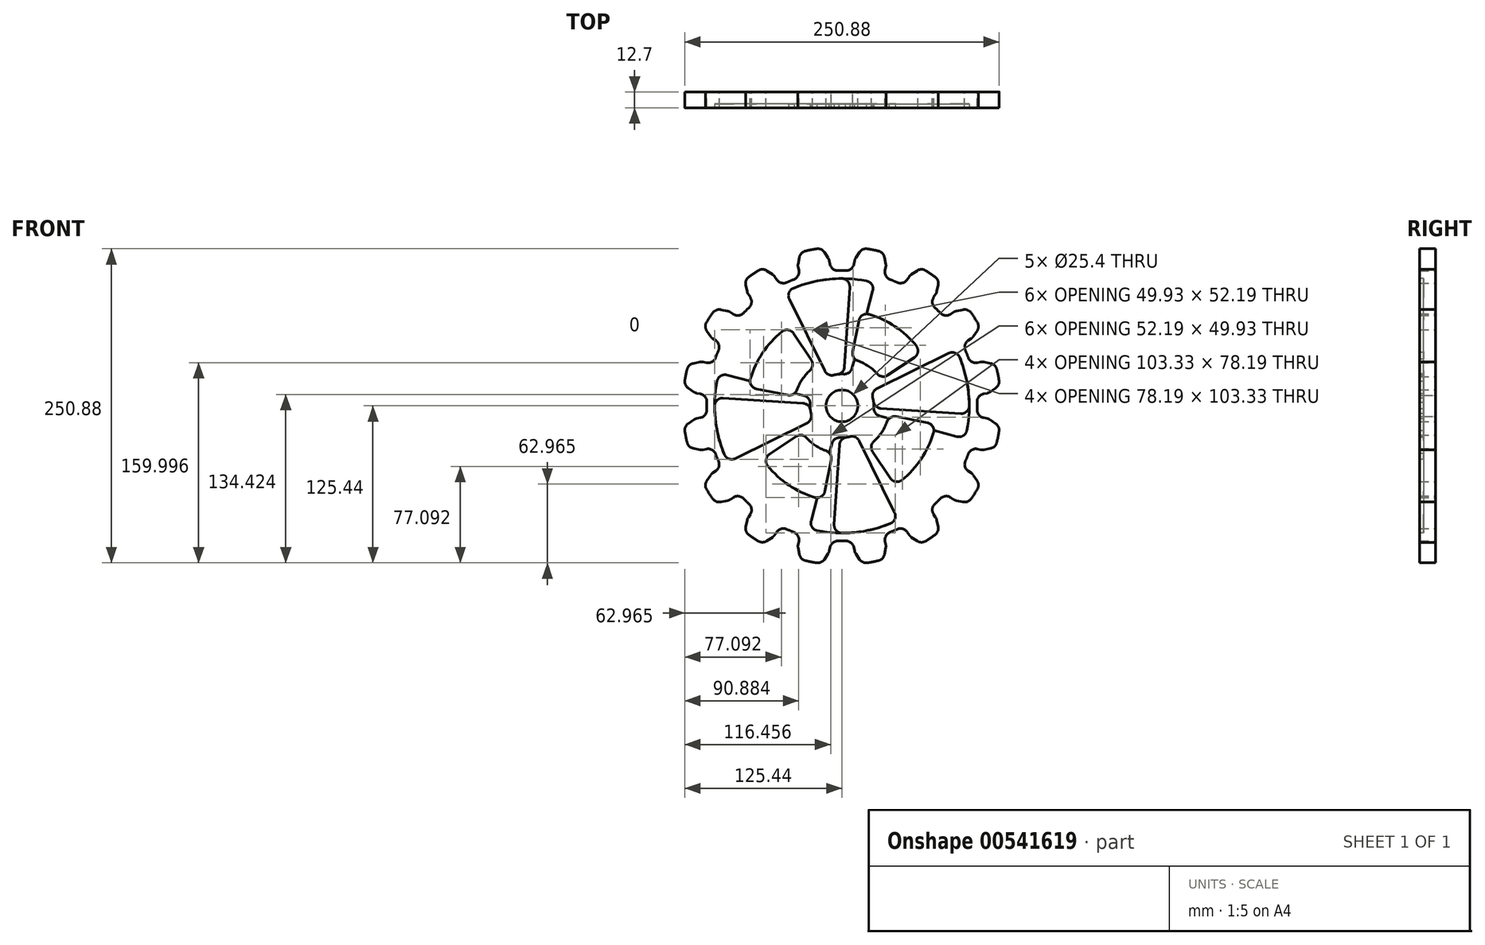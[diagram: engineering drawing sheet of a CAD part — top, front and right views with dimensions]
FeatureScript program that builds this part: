
annotation { "Feature Type Name" : "Feature", "Feature Type Description" : "" }
export const myFeature = defineFeature(function(context is Context, id is Id, definition is map)
    precondition{}
    {
        {
            var Q0;
            Q0=qCreatedBy(makeId("Front.planeOp"),FACE);
            var sketch = newSketch(context, id + "F0", { "sketchPlane" : qUnion([Q0])});
            skArc(sketch, "E0", {"start": v(-57.36, 91.45) * mm, "mid": v(-59.97, 89.76) * mm, "end": v(-62.54, 87.99) * mm});
            skArc(sketch, "E1", {"start": v(-67.46, -35.44) * mm, "mid": v(-53.88, -53.88) * mm, "end": v(-35.44, -67.46) * mm});
            skArc(sketch, "E2", {"start": v(-32.76, -19.46) * mm, "mid": v(-26.94, -26.94) * mm, "end": v(-19.46, -32.76) * mm});
            skLineSegment(sketch, "E3", {"start": v(-16.84, 40.65) * mm, "end": v(-26.62, 64.27) * mm});
            skLineSegment(sketch, "E4", {"start": v(-40.65, -16.84) * mm, "end": v(-64.27, -26.62) * mm});
            skLineSegment(sketch, "E5", {"start": v(-40.65, 16.84) * mm, "end": v(-64.27, 26.62) * mm});
            skLineSegment(sketch, "E6", {"start": v(40.65, -16.84) * mm, "end": v(64.27, -26.62) * mm});
            skLineSegment(sketch, "E7", {"start": v(16.84, 40.65) * mm, "end": v(26.62, 64.27) * mm});
            skLineSegment(sketch, "E8", {"start": v(16.84, -40.65) * mm, "end": v(26.62, -64.27) * mm});
            skLineSegment(sketch, "E9", {"start": v(40.65, 16.84) * mm, "end": v(64.27, 26.62) * mm});
            skLineSegment(sketch, "E10", {"start": v(-16.84, -40.65) * mm, "end": v(-26.62, -64.27) * mm});
            skCircle(sketch, "E11", {"center": v(0, 0) * mm, "radius": 12.7 * mm});
            skArc(sketch, "E12.trimOffspring", {"start": v(-35.44, 67.46) * mm, "mid": v(-53.88, 53.88) * mm, "end": v(-67.46, 35.44) * mm});
            skArc(sketch, "E13.trimOffspring", {"start": v(67.46, 35.44) * mm, "mid": v(53.88, 53.88) * mm, "end": v(35.44, 67.46) * mm});
            skArc(sketch, "E14.trimOffspring", {"start": v(35.44, -67.46) * mm, "mid": v(53.88, -53.88) * mm, "end": v(67.46, -35.44) * mm});
            skArc(sketch, "E15.trimOffspring", {"start": v(19.46, -32.76) * mm, "mid": v(26.94, -26.94) * mm, "end": v(32.76, -19.46) * mm});
            skArc(sketch, "E16.trimOffspring", {"start": v(32.76, 19.46) * mm, "mid": v(26.94, 26.94) * mm, "end": v(19.46, 32.76) * mm});
            skArc(sketch, "E17.trimOffspring", {"start": v(-19.46, 32.76) * mm, "mid": v(-26.94, 26.94) * mm, "end": v(-32.76, 19.46) * mm});
            skPoint(sketch, "E18.visualSharp", {"position": v(-29.16, 70.4) * mm});
            skArc(sketch, "E18.filletArc", {"start": v(-26.62, 64.27) * mm, "mid": v(-30.33, 67.8) * mm, "end": v(-35.44, 67.46) * mm});
            skPoint(sketch, "E19.visualSharp", {"position": v(-70.4, 29.16) * mm});
            skArc(sketch, "E19.filletArc", {"start": v(-67.46, 35.44) * mm, "mid": v(-67.8, 30.33) * mm, "end": v(-64.27, 26.62) * mm});
            skPoint(sketch, "E20.visualSharp", {"position": v(-35.2, 14.58) * mm});
            skArc(sketch, "E20.filletArc", {"start": v(-40.65, 16.84) * mm, "mid": v(-36.21, 16.68) * mm, "end": v(-32.76, 19.46) * mm});
            skPoint(sketch, "E21.visualSharp", {"position": v(-14.58, 35.2) * mm});
            skArc(sketch, "E21.filletArc", {"start": v(-19.46, 32.76) * mm, "mid": v(-16.68, 36.21) * mm, "end": v(-16.84, 40.65) * mm});
            skPoint(sketch, "E22.visualSharp", {"position": v(29.16, 70.4) * mm});
            skArc(sketch, "E22.filletArc", {"start": v(35.44, 67.46) * mm, "mid": v(30.33, 67.8) * mm, "end": v(26.62, 64.27) * mm});
            skPoint(sketch, "E23.visualSharp", {"position": v(70.4, 29.16) * mm});
            skArc(sketch, "E23.filletArc", {"start": v(64.27, 26.62) * mm, "mid": v(67.8, 30.33) * mm, "end": v(67.46, 35.44) * mm});
            skPoint(sketch, "E24.visualSharp", {"position": v(35.2, 14.58) * mm});
            skArc(sketch, "E24.filletArc", {"start": v(32.76, 19.46) * mm, "mid": v(36.21, 16.68) * mm, "end": v(40.65, 16.84) * mm});
            skPoint(sketch, "E25.visualSharp", {"position": v(14.58, 35.2) * mm});
            skArc(sketch, "E25.filletArc", {"start": v(16.84, 40.65) * mm, "mid": v(16.68, 36.21) * mm, "end": v(19.46, 32.76) * mm});
            skPoint(sketch, "E26.visualSharp", {"position": v(-70.4, -29.16) * mm});
            skArc(sketch, "E26.filletArc", {"start": v(-64.27, -26.62) * mm, "mid": v(-67.8, -30.33) * mm, "end": v(-67.46, -35.44) * mm});
            skPoint(sketch, "E27.visualSharp", {"position": v(-29.16, -70.4) * mm});
            skArc(sketch, "E27.filletArc", {"start": v(-35.44, -67.46) * mm, "mid": v(-30.33, -67.8) * mm, "end": v(-26.62, -64.27) * mm});
            skPoint(sketch, "E28.visualSharp", {"position": v(-14.58, -35.2) * mm});
            skArc(sketch, "E28.filletArc", {"start": v(-16.84, -40.65) * mm, "mid": v(-16.68, -36.21) * mm, "end": v(-19.46, -32.76) * mm});
            skPoint(sketch, "E29.visualSharp", {"position": v(-35.2, -14.58) * mm});
            skArc(sketch, "E29.filletArc", {"start": v(-32.76, -19.46) * mm, "mid": v(-36.21, -16.68) * mm, "end": v(-40.65, -16.84) * mm});
            skPoint(sketch, "E30.visualSharp", {"position": v(70.4, -29.16) * mm});
            skArc(sketch, "E30.filletArc", {"start": v(67.46, -35.44) * mm, "mid": v(67.8, -30.33) * mm, "end": v(64.27, -26.62) * mm});
            skPoint(sketch, "E31.visualSharp", {"position": v(29.16, -70.4) * mm});
            skArc(sketch, "E31.filletArc", {"start": v(26.62, -64.27) * mm, "mid": v(30.33, -67.8) * mm, "end": v(35.44, -67.46) * mm});
            skPoint(sketch, "E32.visualSharp", {"position": v(14.58, -35.2) * mm});
            skArc(sketch, "E32.filletArc", {"start": v(19.46, -32.76) * mm, "mid": v(16.68, -36.21) * mm, "end": v(16.84, -40.65) * mm});
            skPoint(sketch, "E33.visualSharp", {"position": v(35.2, -14.58) * mm});
            skArc(sketch, "E33.filletArc", {"start": v(40.65, -16.84) * mm, "mid": v(36.21, -16.68) * mm, "end": v(32.76, -19.46) * mm});
            skLineSegment(sketch, "E34", {"start": v(-12.7, 115.52) * mm, "end": v(-12.7, 112.7) * mm});
            skLineSegment(sketch, "E35", {"start": v(12.7, 115.52) * mm, "end": v(12.7, 112.7) * mm});
            skLineSegment(sketch, "E36", {"start": v(-12.22, 117.95) * mm, "end": v(-10.12, 123) * mm});
            skLineSegment(sketch, "E37", {"start": v(12.22, 117.95) * mm, "end": v(10.12, 123) * mm});
            skArc(sketch, "E38.trimOffspring", {"start": v(4.48, 126.92) * mm, "mid": v(0, 127) * mm, "end": v(-4.48, 126.92) * mm});
            skArc(sketch, "E39.filletArc", {"start": v(-4.48, 126.92) * mm, "mid": v(-7.88, 125.8) * mm, "end": v(-10.12, 123) * mm});
            skArc(sketch, "E40.filletArc", {"start": v(10.12, 123) * mm, "mid": v(7.88, 125.8) * mm, "end": v(4.48, 126.92) * mm});
            skPoint(sketch, "E41.visualSharp", {"position": v(-12.7, 116.78) * mm});
            skArc(sketch, "E41.filletArc", {"start": v(-12.22, 117.95) * mm, "mid": v(-12.58, 116.76) * mm, "end": v(-12.7, 115.52) * mm});
            skPoint(sketch, "E42.visualSharp", {"position": v(12.7, 116.78) * mm});
            skArc(sketch, "E42.filletArc", {"start": v(12.7, 115.52) * mm, "mid": v(12.58, 116.76) * mm, "end": v(12.22, 117.95) * mm});
            skLineSegment(sketch, "E43.1.0", {"start": v(55.94, 101.87) * mm, "end": v(54.86, 99.26) * mm});
            skArc(sketch, "E43.1.1", {"start": v(52.7, 115.55) * mm, "mid": v(48.6, 117.33) * mm, "end": v(44.43, 118.97) * mm});
            skArc(sketch, "E43.1.2", {"start": v(44.43, 118.97) * mm, "mid": v(40.86, 119.23) * mm, "end": v(37.72, 117.52) * mm});
            skArc(sketch, "E43.1.3", {"start": v(56.42, 109.77) * mm, "mid": v(55.41, 113.2) * mm, "end": v(52.7, 115.55) * mm});
            skPoint(sketch, "E43.1.4", {"position": v(32.96, 112.75) * mm});
            skPoint(sketch, "E43.1.5", {"position": v(56.42, 103.03) * mm});
            skLineSegment(sketch, "E43.1.6", {"start": v(32.47, 111.59) * mm, "end": v(31.4, 108.98) * mm});
            skLineSegment(sketch, "E43.1.7", {"start": v(33.85, 113.65) * mm, "end": v(37.72, 117.52) * mm});
            skLineSegment(sketch, "E43.1.8", {"start": v(56.42, 104.3) * mm, "end": v(56.42, 109.77) * mm});
            skArc(sketch, "E43.1.9", {"start": v(55.94, 101.87) * mm, "mid": v(56.3, 103.06) * mm, "end": v(56.42, 104.3) * mm});
            skArc(sketch, "E43.1.10", {"start": v(33.85, 113.65) * mm, "mid": v(33.06, 112.68) * mm, "end": v(32.47, 111.59) * mm});
            skLineSegment(sketch, "E43.2.0", {"start": v(90.66, 72.7) * mm, "end": v(88.67, 70.71) * mm});
            skArc(sketch, "E43.2.1", {"start": v(92.91, 86.58) * mm, "mid": v(89.8, 89.8) * mm, "end": v(86.58, 92.91) * mm});
            skArc(sketch, "E43.2.2", {"start": v(86.58, 92.91) * mm, "mid": v(83.38, 94.52) * mm, "end": v(79.82, 94.14) * mm});
            skArc(sketch, "E43.2.3", {"start": v(94.14, 79.82) * mm, "mid": v(94.52, 83.38) * mm, "end": v(92.91, 86.58) * mm});
            skPoint(sketch, "E43.2.4", {"position": v(73.6, 91.56) * mm});
            skPoint(sketch, "E43.2.5", {"position": v(91.56, 73.6) * mm});
            skLineSegment(sketch, "E43.2.6", {"start": v(72.7, 90.66) * mm, "end": v(70.71, 88.67) * mm});
            skLineSegment(sketch, "E43.2.7", {"start": v(74.76, 92.04) * mm, "end": v(79.82, 94.14) * mm});
            skLineSegment(sketch, "E43.2.8", {"start": v(92.04, 74.76) * mm, "end": v(94.14, 79.82) * mm});
            skArc(sketch, "E43.2.9", {"start": v(90.66, 72.7) * mm, "mid": v(91.45, 73.67) * mm, "end": v(92.04, 74.76) * mm});
            skArc(sketch, "E43.2.10", {"start": v(74.76, 92.04) * mm, "mid": v(73.67, 91.45) * mm, "end": v(72.7, 90.66) * mm});
            skLineSegment(sketch, "E43.3.0", {"start": v(111.59, 32.47) * mm, "end": v(108.98, 31.4) * mm});
            skArc(sketch, "E43.3.1", {"start": v(118.97, 44.43) * mm, "mid": v(117.33, 48.6) * mm, "end": v(115.55, 52.7) * mm});
            skArc(sketch, "E43.3.2", {"start": v(115.55, 52.7) * mm, "mid": v(113.2, 55.41) * mm, "end": v(109.77, 56.42) * mm});
            skArc(sketch, "E43.3.3", {"start": v(117.52, 37.72) * mm, "mid": v(119.23, 40.86) * mm, "end": v(118.97, 44.43) * mm});
            skPoint(sketch, "E43.3.4", {"position": v(103.03, 56.42) * mm});
            skPoint(sketch, "E43.3.5", {"position": v(112.75, 32.96) * mm});
            skLineSegment(sketch, "E43.3.6", {"start": v(101.87, 55.94) * mm, "end": v(99.26, 54.86) * mm});
            skLineSegment(sketch, "E43.3.7", {"start": v(104.3, 56.42) * mm, "end": v(109.77, 56.42) * mm});
            skLineSegment(sketch, "E43.3.8", {"start": v(113.65, 33.85) * mm, "end": v(117.52, 37.72) * mm});
            skArc(sketch, "E43.3.9", {"start": v(111.59, 32.47) * mm, "mid": v(112.68, 33.06) * mm, "end": v(113.65, 33.85) * mm});
            skArc(sketch, "E43.3.10", {"start": v(104.3, 56.42) * mm, "mid": v(103.06, 56.3) * mm, "end": v(101.87, 55.94) * mm});
            skLineSegment(sketch, "E43.4.0", {"start": v(115.52, -12.7) * mm, "end": v(112.7, -12.7) * mm});
            skArc(sketch, "E43.4.1", {"start": v(126.92, -4.48) * mm, "mid": v(127, 0) * mm, "end": v(126.92, 4.48) * mm});
            skArc(sketch, "E43.4.2", {"start": v(126.92, 4.48) * mm, "mid": v(125.8, 7.88) * mm, "end": v(123, 10.12) * mm});
            skArc(sketch, "E43.4.3", {"start": v(123, -10.12) * mm, "mid": v(125.8, -7.88) * mm, "end": v(126.92, -4.48) * mm});
            skPoint(sketch, "E43.4.4", {"position": v(116.78, 12.7) * mm});
            skPoint(sketch, "E43.4.5", {"position": v(116.78, -12.7) * mm});
            skLineSegment(sketch, "E43.4.6", {"start": v(115.52, 12.7) * mm, "end": v(112.7, 12.7) * mm});
            skLineSegment(sketch, "E43.4.7", {"start": v(117.95, 12.22) * mm, "end": v(123, 10.12) * mm});
            skLineSegment(sketch, "E43.4.8", {"start": v(117.95, -12.22) * mm, "end": v(123, -10.12) * mm});
            skArc(sketch, "E43.4.9", {"start": v(115.52, -12.7) * mm, "mid": v(116.76, -12.58) * mm, "end": v(117.95, -12.22) * mm});
            skArc(sketch, "E43.4.10", {"start": v(117.95, 12.22) * mm, "mid": v(116.76, 12.58) * mm, "end": v(115.52, 12.7) * mm});
            skLineSegment(sketch, "E43.5.0", {"start": v(101.87, -55.94) * mm, "end": v(99.26, -54.86) * mm});
            skArc(sketch, "E43.5.1", {"start": v(115.55, -52.7) * mm, "mid": v(117.33, -48.6) * mm, "end": v(118.97, -44.43) * mm});
            skArc(sketch, "E43.5.2", {"start": v(118.97, -44.43) * mm, "mid": v(119.23, -40.86) * mm, "end": v(117.52, -37.72) * mm});
            skArc(sketch, "E43.5.3", {"start": v(109.77, -56.42) * mm, "mid": v(113.2, -55.41) * mm, "end": v(115.55, -52.7) * mm});
            skPoint(sketch, "E43.5.4", {"position": v(112.75, -32.96) * mm});
            skPoint(sketch, "E43.5.5", {"position": v(103.03, -56.42) * mm});
            skLineSegment(sketch, "E43.5.6", {"start": v(111.59, -32.47) * mm, "end": v(108.98, -31.4) * mm});
            skLineSegment(sketch, "E43.5.7", {"start": v(113.65, -33.85) * mm, "end": v(117.52, -37.72) * mm});
            skLineSegment(sketch, "E43.5.8", {"start": v(104.3, -56.42) * mm, "end": v(109.77, -56.42) * mm});
            skArc(sketch, "E43.5.9", {"start": v(101.87, -55.94) * mm, "mid": v(103.06, -56.3) * mm, "end": v(104.3, -56.42) * mm});
            skArc(sketch, "E43.5.10", {"start": v(113.65, -33.85) * mm, "mid": v(112.68, -33.06) * mm, "end": v(111.59, -32.47) * mm});
            skLineSegment(sketch, "E43.6.0", {"start": v(72.7, -90.66) * mm, "end": v(70.71, -88.67) * mm});
            skArc(sketch, "E43.6.1", {"start": v(86.58, -92.91) * mm, "mid": v(89.8, -89.8) * mm, "end": v(92.91, -86.58) * mm});
            skArc(sketch, "E43.6.2", {"start": v(92.91, -86.58) * mm, "mid": v(94.52, -83.38) * mm, "end": v(94.14, -79.82) * mm});
            skArc(sketch, "E43.6.3", {"start": v(79.82, -94.14) * mm, "mid": v(83.38, -94.52) * mm, "end": v(86.58, -92.91) * mm});
            skPoint(sketch, "E43.6.4", {"position": v(91.56, -73.6) * mm});
            skPoint(sketch, "E43.6.5", {"position": v(73.6, -91.56) * mm});
            skLineSegment(sketch, "E43.6.6", {"start": v(90.66, -72.7) * mm, "end": v(88.67, -70.71) * mm});
            skLineSegment(sketch, "E43.6.7", {"start": v(92.04, -74.76) * mm, "end": v(94.14, -79.82) * mm});
            skLineSegment(sketch, "E43.6.8", {"start": v(74.76, -92.04) * mm, "end": v(79.82, -94.14) * mm});
            skArc(sketch, "E43.6.9", {"start": v(72.7, -90.66) * mm, "mid": v(73.67, -91.45) * mm, "end": v(74.76, -92.04) * mm});
            skArc(sketch, "E43.6.10", {"start": v(92.04, -74.76) * mm, "mid": v(91.45, -73.67) * mm, "end": v(90.66, -72.7) * mm});
            skLineSegment(sketch, "E43.7.0", {"start": v(32.47, -111.59) * mm, "end": v(31.4, -108.98) * mm});
            skArc(sketch, "E43.7.1", {"start": v(44.43, -118.97) * mm, "mid": v(48.6, -117.33) * mm, "end": v(52.7, -115.55) * mm});
            skArc(sketch, "E43.7.2", {"start": v(52.7, -115.55) * mm, "mid": v(55.41, -113.2) * mm, "end": v(56.42, -109.77) * mm});
            skArc(sketch, "E43.7.3", {"start": v(37.72, -117.52) * mm, "mid": v(40.86, -119.23) * mm, "end": v(44.43, -118.97) * mm});
            skPoint(sketch, "E43.7.4", {"position": v(56.42, -103.03) * mm});
            skPoint(sketch, "E43.7.5", {"position": v(32.96, -112.75) * mm});
            skLineSegment(sketch, "E43.7.6", {"start": v(55.94, -101.87) * mm, "end": v(54.86, -99.26) * mm});
            skLineSegment(sketch, "E43.7.7", {"start": v(56.42, -104.3) * mm, "end": v(56.42, -109.77) * mm});
            skLineSegment(sketch, "E43.7.8", {"start": v(33.85, -113.65) * mm, "end": v(37.72, -117.52) * mm});
            skArc(sketch, "E43.7.9", {"start": v(32.47, -111.59) * mm, "mid": v(33.06, -112.68) * mm, "end": v(33.85, -113.65) * mm});
            skArc(sketch, "E43.7.10", {"start": v(56.42, -104.3) * mm, "mid": v(56.3, -103.06) * mm, "end": v(55.94, -101.87) * mm});
            skLineSegment(sketch, "E43.8.0", {"start": v(-12.7, -115.52) * mm, "end": v(-12.7, -112.7) * mm});
            skArc(sketch, "E43.8.1", {"start": v(-4.48, -126.92) * mm, "mid": v(0, -127) * mm, "end": v(4.48, -126.92) * mm});
            skArc(sketch, "E43.8.2", {"start": v(4.48, -126.92) * mm, "mid": v(7.88, -125.8) * mm, "end": v(10.12, -123) * mm});
            skArc(sketch, "E43.8.3", {"start": v(-10.12, -123) * mm, "mid": v(-7.88, -125.8) * mm, "end": v(-4.48, -126.92) * mm});
            skPoint(sketch, "E43.8.4", {"position": v(12.7, -116.78) * mm});
            skPoint(sketch, "E43.8.5", {"position": v(-12.7, -116.78) * mm});
            skLineSegment(sketch, "E43.8.6", {"start": v(12.7, -115.52) * mm, "end": v(12.7, -112.7) * mm});
            skLineSegment(sketch, "E43.8.7", {"start": v(12.22, -117.95) * mm, "end": v(10.12, -123) * mm});
            skLineSegment(sketch, "E43.8.8", {"start": v(-12.22, -117.95) * mm, "end": v(-10.12, -123) * mm});
            skArc(sketch, "E43.8.9", {"start": v(-12.7, -115.52) * mm, "mid": v(-12.58, -116.76) * mm, "end": v(-12.22, -117.95) * mm});
            skArc(sketch, "E43.8.10", {"start": v(12.22, -117.95) * mm, "mid": v(12.58, -116.76) * mm, "end": v(12.7, -115.52) * mm});
            skLineSegment(sketch, "E43.9.0", {"start": v(-55.94, -101.87) * mm, "end": v(-54.86, -99.26) * mm});
            skArc(sketch, "E43.9.1", {"start": v(-52.7, -115.55) * mm, "mid": v(-48.6, -117.33) * mm, "end": v(-44.43, -118.97) * mm});
            skArc(sketch, "E43.9.2", {"start": v(-44.43, -118.97) * mm, "mid": v(-40.86, -119.23) * mm, "end": v(-37.72, -117.52) * mm});
            skArc(sketch, "E43.9.3", {"start": v(-56.42, -109.77) * mm, "mid": v(-55.41, -113.2) * mm, "end": v(-52.7, -115.55) * mm});
            skPoint(sketch, "E43.9.4", {"position": v(-32.96, -112.75) * mm});
            skPoint(sketch, "E43.9.5", {"position": v(-56.42, -103.03) * mm});
            skLineSegment(sketch, "E43.9.6", {"start": v(-32.47, -111.59) * mm, "end": v(-31.4, -108.98) * mm});
            skLineSegment(sketch, "E43.9.7", {"start": v(-33.85, -113.65) * mm, "end": v(-37.72, -117.52) * mm});
            skLineSegment(sketch, "E43.9.8", {"start": v(-56.42, -104.3) * mm, "end": v(-56.42, -109.77) * mm});
            skArc(sketch, "E43.9.9", {"start": v(-55.94, -101.87) * mm, "mid": v(-56.3, -103.06) * mm, "end": v(-56.42, -104.3) * mm});
            skArc(sketch, "E43.9.10", {"start": v(-33.85, -113.65) * mm, "mid": v(-33.06, -112.68) * mm, "end": v(-32.47, -111.59) * mm});
            skLineSegment(sketch, "E43.10.0", {"start": v(-90.66, -72.7) * mm, "end": v(-88.67, -70.71) * mm});
            skArc(sketch, "E43.10.1", {"start": v(-92.91, -86.58) * mm, "mid": v(-89.8, -89.8) * mm, "end": v(-86.58, -92.91) * mm});
            skArc(sketch, "E43.10.2", {"start": v(-86.58, -92.91) * mm, "mid": v(-83.38, -94.52) * mm, "end": v(-79.82, -94.14) * mm});
            skArc(sketch, "E43.10.3", {"start": v(-94.14, -79.82) * mm, "mid": v(-94.52, -83.38) * mm, "end": v(-92.91, -86.58) * mm});
            skPoint(sketch, "E43.10.4", {"position": v(-73.6, -91.56) * mm});
            skPoint(sketch, "E43.10.5", {"position": v(-91.56, -73.6) * mm});
            skLineSegment(sketch, "E43.10.6", {"start": v(-72.7, -90.66) * mm, "end": v(-70.71, -88.67) * mm});
            skLineSegment(sketch, "E43.10.7", {"start": v(-74.76, -92.04) * mm, "end": v(-79.82, -94.14) * mm});
            skLineSegment(sketch, "E43.10.8", {"start": v(-92.04, -74.76) * mm, "end": v(-94.14, -79.82) * mm});
            skArc(sketch, "E43.10.9", {"start": v(-90.66, -72.7) * mm, "mid": v(-91.45, -73.67) * mm, "end": v(-92.04, -74.76) * mm});
            skArc(sketch, "E43.10.10", {"start": v(-74.76, -92.04) * mm, "mid": v(-73.67, -91.45) * mm, "end": v(-72.7, -90.66) * mm});
            skLineSegment(sketch, "E43.11.0", {"start": v(-111.59, -32.47) * mm, "end": v(-108.98, -31.4) * mm});
            skArc(sketch, "E43.11.1", {"start": v(-118.97, -44.43) * mm, "mid": v(-117.33, -48.6) * mm, "end": v(-115.55, -52.7) * mm});
            skArc(sketch, "E43.11.2", {"start": v(-115.55, -52.7) * mm, "mid": v(-113.2, -55.41) * mm, "end": v(-109.77, -56.42) * mm});
            skArc(sketch, "E43.11.3", {"start": v(-117.52, -37.72) * mm, "mid": v(-119.23, -40.86) * mm, "end": v(-118.97, -44.43) * mm});
            skPoint(sketch, "E43.11.4", {"position": v(-103.03, -56.42) * mm});
            skPoint(sketch, "E43.11.5", {"position": v(-112.75, -32.96) * mm});
            skLineSegment(sketch, "E43.11.6", {"start": v(-101.87, -55.94) * mm, "end": v(-99.26, -54.86) * mm});
            skLineSegment(sketch, "E43.11.7", {"start": v(-104.3, -56.42) * mm, "end": v(-109.77, -56.42) * mm});
            skLineSegment(sketch, "E43.11.8", {"start": v(-113.65, -33.85) * mm, "end": v(-117.52, -37.72) * mm});
            skArc(sketch, "E43.11.9", {"start": v(-111.59, -32.47) * mm, "mid": v(-112.68, -33.06) * mm, "end": v(-113.65, -33.85) * mm});
            skArc(sketch, "E43.11.10", {"start": v(-104.3, -56.42) * mm, "mid": v(-103.06, -56.3) * mm, "end": v(-101.87, -55.94) * mm});
            skLineSegment(sketch, "E43.12.0", {"start": v(-115.52, 12.7) * mm, "end": v(-112.7, 12.7) * mm});
            skArc(sketch, "E43.12.1", {"start": v(-126.92, 4.48) * mm, "mid": v(-127, 0) * mm, "end": v(-126.92, -4.48) * mm});
            skArc(sketch, "E43.12.2", {"start": v(-126.92, -4.48) * mm, "mid": v(-125.8, -7.88) * mm, "end": v(-123, -10.12) * mm});
            skArc(sketch, "E43.12.3", {"start": v(-123, 10.12) * mm, "mid": v(-125.8, 7.88) * mm, "end": v(-126.92, 4.48) * mm});
            skPoint(sketch, "E43.12.4", {"position": v(-116.78, -12.7) * mm});
            skPoint(sketch, "E43.12.5", {"position": v(-116.78, 12.7) * mm});
            skLineSegment(sketch, "E43.12.6", {"start": v(-115.52, -12.7) * mm, "end": v(-112.7, -12.7) * mm});
            skLineSegment(sketch, "E43.12.7", {"start": v(-117.95, -12.22) * mm, "end": v(-123, -10.12) * mm});
            skLineSegment(sketch, "E43.12.8", {"start": v(-117.95, 12.22) * mm, "end": v(-123, 10.12) * mm});
            skArc(sketch, "E43.12.9", {"start": v(-115.52, 12.7) * mm, "mid": v(-116.76, 12.58) * mm, "end": v(-117.95, 12.22) * mm});
            skArc(sketch, "E43.12.10", {"start": v(-117.95, -12.22) * mm, "mid": v(-116.76, -12.58) * mm, "end": v(-115.52, -12.7) * mm});
            skLineSegment(sketch, "E43.13.0", {"start": v(-101.87, 55.94) * mm, "end": v(-99.26, 54.86) * mm});
            skArc(sketch, "E43.13.1", {"start": v(-115.55, 52.7) * mm, "mid": v(-117.33, 48.6) * mm, "end": v(-118.97, 44.43) * mm});
            skArc(sketch, "E43.13.2", {"start": v(-118.97, 44.43) * mm, "mid": v(-119.23, 40.86) * mm, "end": v(-117.52, 37.72) * mm});
            skArc(sketch, "E43.13.3", {"start": v(-109.77, 56.42) * mm, "mid": v(-113.2, 55.41) * mm, "end": v(-115.55, 52.7) * mm});
            skPoint(sketch, "E43.13.4", {"position": v(-112.75, 32.96) * mm});
            skPoint(sketch, "E43.13.5", {"position": v(-103.03, 56.42) * mm});
            skLineSegment(sketch, "E43.13.6", {"start": v(-111.59, 32.47) * mm, "end": v(-108.98, 31.4) * mm});
            skLineSegment(sketch, "E43.13.7", {"start": v(-113.65, 33.85) * mm, "end": v(-117.52, 37.72) * mm});
            skLineSegment(sketch, "E43.13.8", {"start": v(-104.3, 56.42) * mm, "end": v(-109.77, 56.42) * mm});
            skArc(sketch, "E43.13.9", {"start": v(-101.87, 55.94) * mm, "mid": v(-103.06, 56.3) * mm, "end": v(-104.3, 56.42) * mm});
            skArc(sketch, "E43.13.10", {"start": v(-113.65, 33.85) * mm, "mid": v(-112.68, 33.06) * mm, "end": v(-111.59, 32.47) * mm});
            skLineSegment(sketch, "E43.14.0", {"start": v(-72.7, 90.66) * mm, "end": v(-70.71, 88.67) * mm});
            skArc(sketch, "E43.14.1", {"start": v(-86.58, 92.91) * mm, "mid": v(-89.8, 89.8) * mm, "end": v(-92.91, 86.58) * mm});
            skArc(sketch, "E43.14.2", {"start": v(-92.91, 86.58) * mm, "mid": v(-94.52, 83.38) * mm, "end": v(-94.14, 79.82) * mm});
            skArc(sketch, "E43.14.3", {"start": v(-79.82, 94.14) * mm, "mid": v(-83.38, 94.52) * mm, "end": v(-86.58, 92.91) * mm});
            skPoint(sketch, "E43.14.4", {"position": v(-91.56, 73.6) * mm});
            skPoint(sketch, "E43.14.5", {"position": v(-73.6, 91.56) * mm});
            skLineSegment(sketch, "E43.14.6", {"start": v(-90.66, 72.7) * mm, "end": v(-88.67, 70.71) * mm});
            skLineSegment(sketch, "E43.14.7", {"start": v(-92.04, 74.76) * mm, "end": v(-94.14, 79.82) * mm});
            skLineSegment(sketch, "E43.14.8", {"start": v(-74.76, 92.04) * mm, "end": v(-79.82, 94.14) * mm});
            skArc(sketch, "E43.14.9", {"start": v(-72.7, 90.66) * mm, "mid": v(-73.67, 91.45) * mm, "end": v(-74.76, 92.04) * mm});
            skArc(sketch, "E43.14.10", {"start": v(-92.04, 74.76) * mm, "mid": v(-91.45, 73.67) * mm, "end": v(-90.66, 72.7) * mm});
            skLineSegment(sketch, "E43.15.0", {"start": v(-32.47, 111.59) * mm, "end": v(-31.4, 108.98) * mm});
            skArc(sketch, "E43.15.1", {"start": v(-44.43, 118.97) * mm, "mid": v(-48.6, 117.33) * mm, "end": v(-52.7, 115.55) * mm});
            skArc(sketch, "E43.15.2", {"start": v(-52.7, 115.55) * mm, "mid": v(-55.41, 113.2) * mm, "end": v(-56.42, 109.77) * mm});
            skArc(sketch, "E43.15.3", {"start": v(-37.72, 117.52) * mm, "mid": v(-40.86, 119.23) * mm, "end": v(-44.43, 118.97) * mm});
            skPoint(sketch, "E43.15.4", {"position": v(-56.42, 103.03) * mm});
            skPoint(sketch, "E43.15.5", {"position": v(-32.96, 112.75) * mm});
            skLineSegment(sketch, "E43.15.6", {"start": v(-55.94, 101.87) * mm, "end": v(-54.86, 99.26) * mm});
            skLineSegment(sketch, "E43.15.7", {"start": v(-56.42, 104.3) * mm, "end": v(-56.42, 109.77) * mm});
            skLineSegment(sketch, "E43.15.8", {"start": v(-33.85, 113.65) * mm, "end": v(-37.72, 117.52) * mm});
            skArc(sketch, "E43.15.9", {"start": v(-32.47, 111.59) * mm, "mid": v(-33.06, 112.68) * mm, "end": v(-33.85, 113.65) * mm});
            skArc(sketch, "E43.15.10", {"start": v(-56.42, 104.3) * mm, "mid": v(-56.3, 103.06) * mm, "end": v(-55.94, 101.87) * mm});
            skLineSegment(sketch, "E43.anchor1", {"start": v(0, 0) * mm, "end": v(-12.7, 107.2) * mm, "construction": true});
            skLineSegment(sketch, "E43.anchor2", {"start": v(0, 0) * mm, "end": v(-52.76, 94.18) * mm, "construction": true});
            skArc(sketch, "E44.trimOffspring", {"start": v(-18, 106.44) * mm, "mid": v(-21.06, 105.88) * mm, "end": v(-24.11, 105.22) * mm});
            skArc(sketch, "E45.trimOffspring", {"start": v(24.11, 105.22) * mm, "mid": v(21.06, 105.88) * mm, "end": v(18, 106.44) * mm});
            skArc(sketch, "E46.trimOffspring", {"start": v(62.54, 87.99) * mm, "mid": v(59.97, 89.76) * mm, "end": v(57.36, 91.45) * mm});
            skArc(sketch, "E47.trimOffspring", {"start": v(91.45, 57.36) * mm, "mid": v(89.76, 59.97) * mm, "end": v(87.99, 62.54) * mm});
            skArc(sketch, "E48.trimOffspring", {"start": v(106.44, 18) * mm, "mid": v(105.88, 21.06) * mm, "end": v(105.22, 24.11) * mm});
            skArc(sketch, "E49.trimOffspring", {"start": v(105.22, -24.11) * mm, "mid": v(105.88, -21.06) * mm, "end": v(106.44, -18) * mm});
            skArc(sketch, "E50.trimOffspring", {"start": v(87.99, -62.54) * mm, "mid": v(89.76, -59.97) * mm, "end": v(91.45, -57.36) * mm});
            skArc(sketch, "E51.trimOffspring", {"start": v(57.36, -91.45) * mm, "mid": v(59.97, -89.76) * mm, "end": v(62.54, -87.99) * mm});
            skArc(sketch, "E52.trimOffspring", {"start": v(18, -106.44) * mm, "mid": v(21.06, -105.88) * mm, "end": v(24.11, -105.22) * mm});
            skArc(sketch, "E53.trimOffspring", {"start": v(-24.11, -105.22) * mm, "mid": v(-21.06, -105.88) * mm, "end": v(-18, -106.44) * mm});
            skArc(sketch, "E54.trimOffspring", {"start": v(-62.54, -87.99) * mm, "mid": v(-59.97, -89.76) * mm, "end": v(-57.36, -91.45) * mm});
            skArc(sketch, "E55.trimOffspring", {"start": v(-91.45, -57.36) * mm, "mid": v(-89.76, -59.97) * mm, "end": v(-87.99, -62.54) * mm});
            skArc(sketch, "E56.trimOffspring", {"start": v(-106.44, -18) * mm, "mid": v(-105.88, -21.06) * mm, "end": v(-105.22, -24.11) * mm});
            skArc(sketch, "E57.trimOffspring", {"start": v(-105.22, 24.11) * mm, "mid": v(-105.88, 21.06) * mm, "end": v(-106.44, 18) * mm});
            skArc(sketch, "E58.trimOffspring", {"start": v(-87.99, 62.54) * mm, "mid": v(-89.76, 59.97) * mm, "end": v(-91.45, 57.36) * mm});
            skPoint(sketch, "E59.visualSharp", {"position": v(-66.82, 84.78) * mm});
            skArc(sketch, "E59.filletArc", {"start": v(-70.71, 88.67) * mm, "mid": v(-66.75, 86.83) * mm, "end": v(-62.54, 87.99) * mm});
            skPoint(sketch, "E60.visualSharp", {"position": v(-52.76, 94.18) * mm});
            skArc(sketch, "E60.filletArc", {"start": v(-57.36, 91.45) * mm, "mid": v(-54.68, 94.9) * mm, "end": v(-54.86, 99.26) * mm});
            skPoint(sketch, "E61.visualSharp", {"position": v(-29.3, 103.9) * mm});
            skArc(sketch, "E61.filletArc", {"start": v(-31.4, 108.98) * mm, "mid": v(-28.44, 105.77) * mm, "end": v(-24.11, 105.22) * mm});
            skPoint(sketch, "E62.visualSharp", {"position": v(-12.7, 107.2) * mm});
            skArc(sketch, "E62.filletArc", {"start": v(-18, 106.44) * mm, "mid": v(-14.2, 108.6) * mm, "end": v(-12.7, 112.7) * mm});
            skPoint(sketch, "E63.visualSharp", {"position": v(12.7, 107.2) * mm});
            skArc(sketch, "E63.filletArc", {"start": v(12.7, 112.7) * mm, "mid": v(14.2, 108.6) * mm, "end": v(18, 106.44) * mm});
            skPoint(sketch, "E64.visualSharp", {"position": v(29.3, 103.9) * mm});
            skArc(sketch, "E64.filletArc", {"start": v(24.11, 105.22) * mm, "mid": v(28.44, 105.77) * mm, "end": v(31.4, 108.98) * mm});
            skPoint(sketch, "E65.visualSharp", {"position": v(52.76, 94.18) * mm});
            skArc(sketch, "E65.filletArc", {"start": v(54.86, 99.26) * mm, "mid": v(54.68, 94.9) * mm, "end": v(57.36, 91.45) * mm});
            skPoint(sketch, "E66.visualSharp", {"position": v(66.82, 84.78) * mm});
            skArc(sketch, "E66.filletArc", {"start": v(62.54, 87.99) * mm, "mid": v(66.75, 86.83) * mm, "end": v(70.71, 88.67) * mm});
            skPoint(sketch, "E67.visualSharp", {"position": v(84.78, 66.82) * mm});
            skArc(sketch, "E67.filletArc", {"start": v(88.67, 70.71) * mm, "mid": v(86.83, 66.75) * mm, "end": v(87.99, 62.54) * mm});
            skPoint(sketch, "E68.visualSharp", {"position": v(94.18, 52.76) * mm});
            skArc(sketch, "E68.filletArc", {"start": v(91.45, 57.36) * mm, "mid": v(94.9, 54.68) * mm, "end": v(99.26, 54.86) * mm});
            skPoint(sketch, "E69.visualSharp", {"position": v(103.9, 29.3) * mm});
            skArc(sketch, "E69.filletArc", {"start": v(108.98, 31.4) * mm, "mid": v(105.77, 28.44) * mm, "end": v(105.22, 24.11) * mm});
            skPoint(sketch, "E70.visualSharp", {"position": v(107.2, 12.7) * mm});
            skArc(sketch, "E70.filletArc", {"start": v(106.44, 18) * mm, "mid": v(108.6, 14.2) * mm, "end": v(112.7, 12.7) * mm});
            skPoint(sketch, "E71.visualSharp", {"position": v(107.2, -12.7) * mm});
            skArc(sketch, "E71.filletArc", {"start": v(112.7, -12.7) * mm, "mid": v(108.6, -14.2) * mm, "end": v(106.44, -18) * mm});
            skPoint(sketch, "E72.visualSharp", {"position": v(103.9, -29.3) * mm});
            skArc(sketch, "E72.filletArc", {"start": v(105.22, -24.11) * mm, "mid": v(105.77, -28.44) * mm, "end": v(108.98, -31.4) * mm});
            skPoint(sketch, "E73.visualSharp", {"position": v(94.18, -52.76) * mm});
            skArc(sketch, "E73.filletArc", {"start": v(99.26, -54.86) * mm, "mid": v(94.9, -54.68) * mm, "end": v(91.45, -57.36) * mm});
            skPoint(sketch, "E74.visualSharp", {"position": v(84.78, -66.82) * mm});
            skArc(sketch, "E74.filletArc", {"start": v(87.99, -62.54) * mm, "mid": v(86.83, -66.75) * mm, "end": v(88.67, -70.71) * mm});
            skPoint(sketch, "E75.visualSharp", {"position": v(66.82, -84.78) * mm});
            skArc(sketch, "E75.filletArc", {"start": v(70.71, -88.67) * mm, "mid": v(66.75, -86.83) * mm, "end": v(62.54, -87.99) * mm});
            skPoint(sketch, "E76.visualSharp", {"position": v(52.76, -94.18) * mm});
            skArc(sketch, "E76.filletArc", {"start": v(57.36, -91.45) * mm, "mid": v(54.68, -94.9) * mm, "end": v(54.86, -99.26) * mm});
            skPoint(sketch, "E77.visualSharp", {"position": v(29.3, -103.9) * mm});
            skArc(sketch, "E77.filletArc", {"start": v(31.4, -108.98) * mm, "mid": v(28.44, -105.77) * mm, "end": v(24.11, -105.22) * mm});
            skPoint(sketch, "E78.visualSharp", {"position": v(12.7, -107.2) * mm});
            skArc(sketch, "E78.filletArc", {"start": v(18, -106.44) * mm, "mid": v(14.2, -108.6) * mm, "end": v(12.7, -112.7) * mm});
            skPoint(sketch, "E79.visualSharp", {"position": v(-12.7, -107.2) * mm});
            skArc(sketch, "E79.filletArc", {"start": v(-12.7, -112.7) * mm, "mid": v(-14.2, -108.6) * mm, "end": v(-18, -106.44) * mm});
            skPoint(sketch, "E80.visualSharp", {"position": v(-29.3, -103.9) * mm});
            skArc(sketch, "E80.filletArc", {"start": v(-24.11, -105.22) * mm, "mid": v(-28.44, -105.77) * mm, "end": v(-31.4, -108.98) * mm});
            skPoint(sketch, "E81.visualSharp", {"position": v(-52.76, -94.18) * mm});
            skArc(sketch, "E81.filletArc", {"start": v(-54.86, -99.26) * mm, "mid": v(-54.68, -94.9) * mm, "end": v(-57.36, -91.45) * mm});
            skPoint(sketch, "E82.visualSharp", {"position": v(-66.82, -84.78) * mm});
            skArc(sketch, "E82.filletArc", {"start": v(-62.54, -87.99) * mm, "mid": v(-66.75, -86.83) * mm, "end": v(-70.71, -88.67) * mm});
            skPoint(sketch, "E83.visualSharp", {"position": v(-84.78, -66.82) * mm});
            skArc(sketch, "E83.filletArc", {"start": v(-88.67, -70.71) * mm, "mid": v(-86.83, -66.75) * mm, "end": v(-87.99, -62.54) * mm});
            skPoint(sketch, "E84.visualSharp", {"position": v(-94.18, -52.76) * mm});
            skArc(sketch, "E84.filletArc", {"start": v(-91.45, -57.36) * mm, "mid": v(-94.9, -54.68) * mm, "end": v(-99.26, -54.86) * mm});
            skPoint(sketch, "E85.visualSharp", {"position": v(-103.9, -29.3) * mm});
            skArc(sketch, "E85.filletArc", {"start": v(-108.98, -31.4) * mm, "mid": v(-105.77, -28.44) * mm, "end": v(-105.22, -24.11) * mm});
            skPoint(sketch, "E86.visualSharp", {"position": v(-107.2, -12.7) * mm});
            skArc(sketch, "E86.filletArc", {"start": v(-106.44, -18) * mm, "mid": v(-108.6, -14.2) * mm, "end": v(-112.7, -12.7) * mm});
            skPoint(sketch, "E87.visualSharp", {"position": v(-107.2, 12.7) * mm});
            skArc(sketch, "E87.filletArc", {"start": v(-112.7, 12.7) * mm, "mid": v(-108.6, 14.2) * mm, "end": v(-106.44, 18) * mm});
            skPoint(sketch, "E88.visualSharp", {"position": v(-103.9, 29.3) * mm});
            skArc(sketch, "E88.filletArc", {"start": v(-105.22, 24.11) * mm, "mid": v(-105.77, 28.44) * mm, "end": v(-108.98, 31.4) * mm});
            skPoint(sketch, "E89.visualSharp", {"position": v(-94.18, 52.76) * mm});
            skArc(sketch, "E89.filletArc", {"start": v(-99.26, 54.86) * mm, "mid": v(-94.9, 54.68) * mm, "end": v(-91.45, 57.36) * mm});
            skPoint(sketch, "E90.visualSharp", {"position": v(-84.78, 66.82) * mm});
            skArc(sketch, "E90.filletArc", {"start": v(-87.99, 62.54) * mm, "mid": v(-86.83, 66.75) * mm, "end": v(-88.67, 70.71) * mm});
            skSolve(sketch);
        }
        {
            var Q0;
            Q0=qSketchRegion(id+"F0",true);
            extrude(context, id + "F1", {"entities" : qUnion([Q0]), "endBound" : BoundingType.SYMMETRIC, "depth" : 12.7 * mm, "offsetDistance" : 25.4 * mm});
        }
        {
            var Q0;
            Q0=makeQuery(id+"F1.opExtrude","CAP_FACE",FACE,{"disambiguationData":[OSD([sQuery(id+"F0.wireOp",EDGE,"E0"),sQuery(id+"F0.wireOp",EDGE,"E1"),sQuery(id+"F0.wireOp",EDGE,"E2"),sQuery(id+"F0.wireOp",EDGE,"E3"),sQuery(id+"F0.wireOp",EDGE,"E4"),sQuery(id+"F0.wireOp",EDGE,"E5"),sQuery(id+"F0.wireOp",EDGE,"E6"),sQuery(id+"F0.wireOp",EDGE,"E7"),sQuery(id+"F0.wireOp",EDGE,"E8"),sQuery(id+"F0.wireOp",EDGE,"E9"),sQuery(id+"F0.wireOp",EDGE,"E10"),sQuery(id+"F0.wireOp",EDGE,"E11"),sQuery(id+"F0.wireOp",EDGE,"E12.trimOffspring"),sQuery(id+"F0.wireOp",EDGE,"E13.trimOffspring"),sQuery(id+"F0.wireOp",EDGE,"E14.trimOffspring"),sQuery(id+"F0.wireOp",EDGE,"E15.trimOffspring"),sQuery(id+"F0.wireOp",EDGE,"E16.trimOffspring"),sQuery(id+"F0.wireOp",EDGE,"E17.trimOffspring"),sQuery(id+"F0.wireOp",EDGE,"E18.filletArc"),sQuery(id+"F0.wireOp",EDGE,"E19.filletArc"),sQuery(id+"F0.wireOp",EDGE,"E20.filletArc"),sQuery(id+"F0.wireOp",EDGE,"E21.filletArc"),sQuery(id+"F0.wireOp",EDGE,"E22.filletArc"),sQuery(id+"F0.wireOp",EDGE,"E23.filletArc"),sQuery(id+"F0.wireOp",EDGE,"E24.filletArc"),sQuery(id+"F0.wireOp",EDGE,"E25.filletArc"),sQuery(id+"F0.wireOp",EDGE,"E26.filletArc"),sQuery(id+"F0.wireOp",EDGE,"E27.filletArc"),sQuery(id+"F0.wireOp",EDGE,"E28.filletArc"),sQuery(id+"F0.wireOp",EDGE,"E29.filletArc"),sQuery(id+"F0.wireOp",EDGE,"E30.filletArc"),sQuery(id+"F0.wireOp",EDGE,"E31.filletArc"),sQuery(id+"F0.wireOp",EDGE,"E32.filletArc"),sQuery(id+"F0.wireOp",EDGE,"E33.filletArc"),sQuery(id+"F0.wireOp",EDGE,"E34"),sQuery(id+"F0.wireOp",EDGE,"E35"),sQuery(id+"F0.wireOp",EDGE,"E36"),sQuery(id+"F0.wireOp",EDGE,"E37"),sQuery(id+"F0.wireOp",EDGE,"E38.trimOffspring"),sQuery(id+"F0.wireOp",EDGE,"E39.filletArc"),sQuery(id+"F0.wireOp",EDGE,"E40.filletArc"),sQuery(id+"F0.wireOp",EDGE,"E41.filletArc"),sQuery(id+"F0.wireOp",EDGE,"E42.filletArc"),sQuery(id+"F0.wireOp",EDGE,"E43.1.0"),sQuery(id+"F0.wireOp",EDGE,"E43.1.1"),sQuery(id+"F0.wireOp",EDGE,"E43.1.2"),sQuery(id+"F0.wireOp",EDGE,"E43.1.3"),sQuery(id+"F0.wireOp",EDGE,"E43.1.6"),sQuery(id+"F0.wireOp",EDGE,"E43.1.7"),sQuery(id+"F0.wireOp",EDGE,"E43.1.8"),sQuery(id+"F0.wireOp",EDGE,"E43.1.9"),sQuery(id+"F0.wireOp",EDGE,"E43.1.10"),sQuery(id+"F0.wireOp",EDGE,"E43.2.0"),sQuery(id+"F0.wireOp",EDGE,"E43.2.1"),sQuery(id+"F0.wireOp",EDGE,"E43.2.2"),sQuery(id+"F0.wireOp",EDGE,"E43.2.3"),sQuery(id+"F0.wireOp",EDGE,"E43.2.6"),sQuery(id+"F0.wireOp",EDGE,"E43.2.7"),sQuery(id+"F0.wireOp",EDGE,"E43.2.8"),sQuery(id+"F0.wireOp",EDGE,"E43.2.9"),sQuery(id+"F0.wireOp",EDGE,"E43.2.10"),sQuery(id+"F0.wireOp",EDGE,"E43.3.0"),sQuery(id+"F0.wireOp",EDGE,"E43.3.1"),sQuery(id+"F0.wireOp",EDGE,"E43.3.2"),sQuery(id+"F0.wireOp",EDGE,"E43.3.3"),sQuery(id+"F0.wireOp",EDGE,"E43.3.6"),sQuery(id+"F0.wireOp",EDGE,"E43.3.7"),sQuery(id+"F0.wireOp",EDGE,"E43.3.8"),sQuery(id+"F0.wireOp",EDGE,"E43.3.9"),sQuery(id+"F0.wireOp",EDGE,"E43.3.10"),sQuery(id+"F0.wireOp",EDGE,"E43.4.0"),sQuery(id+"F0.wireOp",EDGE,"E43.4.1"),sQuery(id+"F0.wireOp",EDGE,"E43.4.2"),sQuery(id+"F0.wireOp",EDGE,"E43.4.3"),sQuery(id+"F0.wireOp",EDGE,"E43.4.6"),sQuery(id+"F0.wireOp",EDGE,"E43.4.7"),sQuery(id+"F0.wireOp",EDGE,"E43.4.8"),sQuery(id+"F0.wireOp",EDGE,"E43.4.9"),sQuery(id+"F0.wireOp",EDGE,"E43.4.10"),sQuery(id+"F0.wireOp",EDGE,"E43.5.0"),sQuery(id+"F0.wireOp",EDGE,"E43.5.1"),sQuery(id+"F0.wireOp",EDGE,"E43.5.2"),sQuery(id+"F0.wireOp",EDGE,"E43.5.3"),sQuery(id+"F0.wireOp",EDGE,"E43.5.6"),sQuery(id+"F0.wireOp",EDGE,"E43.5.7"),sQuery(id+"F0.wireOp",EDGE,"E43.5.8"),sQuery(id+"F0.wireOp",EDGE,"E43.5.9"),sQuery(id+"F0.wireOp",EDGE,"E43.5.10"),sQuery(id+"F0.wireOp",EDGE,"E43.6.0"),sQuery(id+"F0.wireOp",EDGE,"E43.6.1"),sQuery(id+"F0.wireOp",EDGE,"E43.6.2"),sQuery(id+"F0.wireOp",EDGE,"E43.6.3"),sQuery(id+"F0.wireOp",EDGE,"E43.6.6"),sQuery(id+"F0.wireOp",EDGE,"E43.6.7"),sQuery(id+"F0.wireOp",EDGE,"E43.6.8"),sQuery(id+"F0.wireOp",EDGE,"E43.6.9"),sQuery(id+"F0.wireOp",EDGE,"E43.6.10"),sQuery(id+"F0.wireOp",EDGE,"E43.7.0"),sQuery(id+"F0.wireOp",EDGE,"E43.7.1"),sQuery(id+"F0.wireOp",EDGE,"E43.7.2"),sQuery(id+"F0.wireOp",EDGE,"E43.7.3"),sQuery(id+"F0.wireOp",EDGE,"E43.7.6"),sQuery(id+"F0.wireOp",EDGE,"E43.7.7"),sQuery(id+"F0.wireOp",EDGE,"E43.7.8"),sQuery(id+"F0.wireOp",EDGE,"E43.7.9"),sQuery(id+"F0.wireOp",EDGE,"E43.7.10"),sQuery(id+"F0.wireOp",EDGE,"E43.8.0"),sQuery(id+"F0.wireOp",EDGE,"E43.8.1"),sQuery(id+"F0.wireOp",EDGE,"E43.8.2"),sQuery(id+"F0.wireOp",EDGE,"E43.8.3"),sQuery(id+"F0.wireOp",EDGE,"E43.8.6"),sQuery(id+"F0.wireOp",EDGE,"E43.8.7"),sQuery(id+"F0.wireOp",EDGE,"E43.8.8"),sQuery(id+"F0.wireOp",EDGE,"E43.8.9"),sQuery(id+"F0.wireOp",EDGE,"E43.8.10"),sQuery(id+"F0.wireOp",EDGE,"E43.9.0"),sQuery(id+"F0.wireOp",EDGE,"E43.9.1"),sQuery(id+"F0.wireOp",EDGE,"E43.9.2"),sQuery(id+"F0.wireOp",EDGE,"E43.9.3"),sQuery(id+"F0.wireOp",EDGE,"E43.9.6"),sQuery(id+"F0.wireOp",EDGE,"E43.9.7"),sQuery(id+"F0.wireOp",EDGE,"E43.9.8"),sQuery(id+"F0.wireOp",EDGE,"E43.9.9"),sQuery(id+"F0.wireOp",EDGE,"E43.9.10"),sQuery(id+"F0.wireOp",EDGE,"E43.10.0"),sQuery(id+"F0.wireOp",EDGE,"E43.10.1"),sQuery(id+"F0.wireOp",EDGE,"E43.10.2"),sQuery(id+"F0.wireOp",EDGE,"E43.10.3"),sQuery(id+"F0.wireOp",EDGE,"E43.10.6"),sQuery(id+"F0.wireOp",EDGE,"E43.10.7"),sQuery(id+"F0.wireOp",EDGE,"E43.10.8"),sQuery(id+"F0.wireOp",EDGE,"E43.10.9"),sQuery(id+"F0.wireOp",EDGE,"E43.10.10"),sQuery(id+"F0.wireOp",EDGE,"E43.11.0"),sQuery(id+"F0.wireOp",EDGE,"E43.11.1"),sQuery(id+"F0.wireOp",EDGE,"E43.11.2"),sQuery(id+"F0.wireOp",EDGE,"E43.11.3"),sQuery(id+"F0.wireOp",EDGE,"E43.11.6"),sQuery(id+"F0.wireOp",EDGE,"E43.11.7"),sQuery(id+"F0.wireOp",EDGE,"E43.11.8"),sQuery(id+"F0.wireOp",EDGE,"E43.11.9"),sQuery(id+"F0.wireOp",EDGE,"E43.11.10"),sQuery(id+"F0.wireOp",EDGE,"E43.12.0"),sQuery(id+"F0.wireOp",EDGE,"E43.12.1"),sQuery(id+"F0.wireOp",EDGE,"E43.12.2"),sQuery(id+"F0.wireOp",EDGE,"E43.12.3"),sQuery(id+"F0.wireOp",EDGE,"E43.12.6"),sQuery(id+"F0.wireOp",EDGE,"E43.12.7"),sQuery(id+"F0.wireOp",EDGE,"E43.12.8"),sQuery(id+"F0.wireOp",EDGE,"E43.12.9"),sQuery(id+"F0.wireOp",EDGE,"E43.12.10"),sQuery(id+"F0.wireOp",EDGE,"E43.13.0"),sQuery(id+"F0.wireOp",EDGE,"E43.13.1"),sQuery(id+"F0.wireOp",EDGE,"E43.13.2"),sQuery(id+"F0.wireOp",EDGE,"E43.13.3"),sQuery(id+"F0.wireOp",EDGE,"E43.13.6"),sQuery(id+"F0.wireOp",EDGE,"E43.13.7"),sQuery(id+"F0.wireOp",EDGE,"E43.13.8"),sQuery(id+"F0.wireOp",EDGE,"E43.13.9"),sQuery(id+"F0.wireOp",EDGE,"E43.13.10"),sQuery(id+"F0.wireOp",EDGE,"E43.14.0"),sQuery(id+"F0.wireOp",EDGE,"E43.14.1"),sQuery(id+"F0.wireOp",EDGE,"E43.14.2"),sQuery(id+"F0.wireOp",EDGE,"E43.14.3"),sQuery(id+"F0.wireOp",EDGE,"E43.14.6"),sQuery(id+"F0.wireOp",EDGE,"E43.14.7"),sQuery(id+"F0.wireOp",EDGE,"E43.14.8"),sQuery(id+"F0.wireOp",EDGE,"E43.14.9"),sQuery(id+"F0.wireOp",EDGE,"E43.14.10"),sQuery(id+"F0.wireOp",EDGE,"E43.15.0"),sQuery(id+"F0.wireOp",EDGE,"E43.15.1"),sQuery(id+"F0.wireOp",EDGE,"E43.15.2"),sQuery(id+"F0.wireOp",EDGE,"E43.15.3"),sQuery(id+"F0.wireOp",EDGE,"E43.15.6"),sQuery(id+"F0.wireOp",EDGE,"E43.15.7"),sQuery(id+"F0.wireOp",EDGE,"E43.15.8"),sQuery(id+"F0.wireOp",EDGE,"E43.15.9"),sQuery(id+"F0.wireOp",EDGE,"E43.15.10"),sQuery(id+"F0.wireOp",EDGE,"E44.trimOffspring"),sQuery(id+"F0.wireOp",EDGE,"E45.trimOffspring"),sQuery(id+"F0.wireOp",EDGE,"E46.trimOffspring"),sQuery(id+"F0.wireOp",EDGE,"E47.trimOffspring"),sQuery(id+"F0.wireOp",EDGE,"E48.trimOffspring"),sQuery(id+"F0.wireOp",EDGE,"E49.trimOffspring"),sQuery(id+"F0.wireOp",EDGE,"E50.trimOffspring"),sQuery(id+"F0.wireOp",EDGE,"E51.trimOffspring"),sQuery(id+"F0.wireOp",EDGE,"E52.trimOffspring"),sQuery(id+"F0.wireOp",EDGE,"E53.trimOffspring"),sQuery(id+"F0.wireOp",EDGE,"E54.trimOffspring"),sQuery(id+"F0.wireOp",EDGE,"E55.trimOffspring"),sQuery(id+"F0.wireOp",EDGE,"E56.trimOffspring"),sQuery(id+"F0.wireOp",EDGE,"E57.trimOffspring"),sQuery(id+"F0.wireOp",EDGE,"E58.trimOffspring"),sQuery(id+"F0.wireOp",EDGE,"E59.filletArc"),sQuery(id+"F0.wireOp",EDGE,"E60.filletArc"),sQuery(id+"F0.wireOp",EDGE,"E61.filletArc"),sQuery(id+"F0.wireOp",EDGE,"E62.filletArc"),sQuery(id+"F0.wireOp",EDGE,"E63.filletArc"),sQuery(id+"F0.wireOp",EDGE,"E64.filletArc"),sQuery(id+"F0.wireOp",EDGE,"E65.filletArc"),sQuery(id+"F0.wireOp",EDGE,"E66.filletArc"),sQuery(id+"F0.wireOp",EDGE,"E67.filletArc"),sQuery(id+"F0.wireOp",EDGE,"E68.filletArc"),sQuery(id+"F0.wireOp",EDGE,"E69.filletArc"),sQuery(id+"F0.wireOp",EDGE,"E70.filletArc"),sQuery(id+"F0.wireOp",EDGE,"E71.filletArc"),sQuery(id+"F0.wireOp",EDGE,"E72.filletArc"),sQuery(id+"F0.wireOp",EDGE,"E73.filletArc"),sQuery(id+"F0.wireOp",EDGE,"E74.filletArc"),sQuery(id+"F0.wireOp",EDGE,"E75.filletArc"),sQuery(id+"F0.wireOp",EDGE,"E76.filletArc"),sQuery(id+"F0.wireOp",EDGE,"E77.filletArc"),sQuery(id+"F0.wireOp",EDGE,"E78.filletArc"),sQuery(id+"F0.wireOp",EDGE,"E79.filletArc"),sQuery(id+"F0.wireOp",EDGE,"E80.filletArc"),sQuery(id+"F0.wireOp",EDGE,"E81.filletArc"),sQuery(id+"F0.wireOp",EDGE,"E82.filletArc"),sQuery(id+"F0.wireOp",EDGE,"E83.filletArc"),sQuery(id+"F0.wireOp",EDGE,"E84.filletArc"),sQuery(id+"F0.wireOp",EDGE,"E85.filletArc"),sQuery(id+"F0.wireOp",EDGE,"E86.filletArc"),sQuery(id+"F0.wireOp",EDGE,"E87.filletArc"),sQuery(id+"F0.wireOp",EDGE,"E88.filletArc"),sQuery(id+"F0.wireOp",EDGE,"E89.filletArc"),sQuery(id+"F0.wireOp",EDGE,"E90.filletArc")])],"isStart":false});
            var sketch = newSketch(context, id + "F2", { "sketchPlane" : qUnion([Q0])});
            skArc(sketch, "E91", {"start": v(19.7, 99.67) * mm, "mid": v(0, 101.6) * mm, "end": v(-19.7, 99.67) * mm});
            skArc(sketch, "E92", {"start": v(1.53, 25.35) * mm, "mid": v(0, 25.4) * mm, "end": v(-1.53, 25.35) * mm});
            skLineSegment(sketch, "E93", {"start": v(-8.05, 30.05) * mm, "end": v(-24.6, 91.8) * mm});
            skLineSegment(sketch, "E94", {"start": v(8.05, 30.05) * mm, "end": v(24.6, 91.8) * mm});
            skLineSegment(sketch, "E95", {"start": v(-8.05, -30.05) * mm, "end": v(-24.6, -91.8) * mm});
            skLineSegment(sketch, "E96", {"start": v(8.05, -30.05) * mm, "end": v(24.6, -91.8) * mm});
            skLineSegment(sketch, "E97", {"start": v(30.05, 8.05) * mm, "end": v(91.8, 24.6) * mm});
            skLineSegment(sketch, "E98", {"start": v(30.05, -8.05) * mm, "end": v(91.8, -24.6) * mm});
            skLineSegment(sketch, "E99", {"start": v(-30.05, -8.05) * mm, "end": v(-91.8, -24.6) * mm});
            skLineSegment(sketch, "E100", {"start": v(-30.05, 8.05) * mm, "end": v(-91.8, 24.6) * mm});
            skArc(sketch, "E101.trimOffspring", {"start": v(99.67, -19.7) * mm, "mid": v(101.6, 0) * mm, "end": v(99.67, 19.7) * mm});
            skArc(sketch, "E102.trimOffspring", {"start": v(-19.7, -99.67) * mm, "mid": v(0, -101.6) * mm, "end": v(19.7, -99.67) * mm});
            skArc(sketch, "E103.trimOffspring", {"start": v(-99.67, 19.7) * mm, "mid": v(-101.6, 0) * mm, "end": v(-99.67, -19.7) * mm});
            skArc(sketch, "E104.trimOffspring", {"start": v(25.35, -1.53) * mm, "mid": v(25.4, 0) * mm, "end": v(25.35, 1.53) * mm});
            skArc(sketch, "E105.trimOffspring", {"start": v(-1.53, -25.35) * mm, "mid": v(0, -25.4) * mm, "end": v(1.53, -25.35) * mm});
            skArc(sketch, "E106.trimOffspring", {"start": v(-25.35, 1.53) * mm, "mid": v(-25.4, 0) * mm, "end": v(-25.35, -1.53) * mm});
            skPoint(sketch, "E107.visualSharp", {"position": v(-26.3, 98.14) * mm});
            skArc(sketch, "E107.filletArc", {"start": v(-19.7, 99.67) * mm, "mid": v(-23.85, 96.8) * mm, "end": v(-24.6, 91.8) * mm});
            skPoint(sketch, "E108.visualSharp", {"position": v(26.3, 98.14) * mm});
            skArc(sketch, "E108.filletArc", {"start": v(24.6, 91.8) * mm, "mid": v(23.85, 96.8) * mm, "end": v(19.7, 99.67) * mm});
            skPoint(sketch, "E109.visualSharp", {"position": v(-6.57, 24.53) * mm});
            skArc(sketch, "E109.filletArc", {"start": v(-8.05, 30.05) * mm, "mid": v(-5.63, 26.54) * mm, "end": v(-1.53, 25.35) * mm});
            skPoint(sketch, "E110.visualSharp", {"position": v(6.57, 24.53) * mm});
            skArc(sketch, "E110.filletArc", {"start": v(1.53, 25.35) * mm, "mid": v(5.63, 26.54) * mm, "end": v(8.05, 30.05) * mm});
            skPoint(sketch, "E111.visualSharp", {"position": v(98.14, 26.3) * mm});
            skArc(sketch, "E111.filletArc", {"start": v(99.67, 19.7) * mm, "mid": v(96.8, 23.85) * mm, "end": v(91.8, 24.6) * mm});
            skPoint(sketch, "E112.visualSharp", {"position": v(98.14, -26.3) * mm});
            skArc(sketch, "E112.filletArc", {"start": v(91.8, -24.6) * mm, "mid": v(96.8, -23.85) * mm, "end": v(99.67, -19.7) * mm});
            skPoint(sketch, "E113.visualSharp", {"position": v(24.53, 6.57) * mm});
            skArc(sketch, "E113.filletArc", {"start": v(30.05, 8.05) * mm, "mid": v(26.54, 5.63) * mm, "end": v(25.35, 1.53) * mm});
            skPoint(sketch, "E114.visualSharp", {"position": v(24.53, -6.57) * mm});
            skArc(sketch, "E114.filletArc", {"start": v(25.35, -1.53) * mm, "mid": v(26.54, -5.63) * mm, "end": v(30.05, -8.05) * mm});
            skPoint(sketch, "E115.visualSharp", {"position": v(-24.53, 6.57) * mm});
            skArc(sketch, "E115.filletArc", {"start": v(-25.35, 1.53) * mm, "mid": v(-26.54, 5.63) * mm, "end": v(-30.05, 8.05) * mm});
            skPoint(sketch, "E116.visualSharp", {"position": v(-24.53, -6.57) * mm});
            skArc(sketch, "E116.filletArc", {"start": v(-30.05, -8.05) * mm, "mid": v(-26.54, -5.63) * mm, "end": v(-25.35, -1.53) * mm});
            skPoint(sketch, "E117.visualSharp", {"position": v(-98.14, -26.3) * mm});
            skArc(sketch, "E117.filletArc", {"start": v(-99.67, -19.7) * mm, "mid": v(-96.8, -23.85) * mm, "end": v(-91.8, -24.6) * mm});
            skPoint(sketch, "E118.visualSharp", {"position": v(-98.14, 26.3) * mm});
            skArc(sketch, "E118.filletArc", {"start": v(-91.8, 24.6) * mm, "mid": v(-96.8, 23.85) * mm, "end": v(-99.67, 19.7) * mm});
            skPoint(sketch, "E119.visualSharp", {"position": v(-6.57, -24.53) * mm});
            skArc(sketch, "E119.filletArc", {"start": v(-1.53, -25.35) * mm, "mid": v(-5.63, -26.54) * mm, "end": v(-8.05, -30.05) * mm});
            skPoint(sketch, "E120.visualSharp", {"position": v(6.57, -24.53) * mm});
            skArc(sketch, "E120.filletArc", {"start": v(8.05, -30.05) * mm, "mid": v(5.63, -26.54) * mm, "end": v(1.53, -25.35) * mm});
            skPoint(sketch, "E121.visualSharp", {"position": v(26.3, -98.14) * mm});
            skArc(sketch, "E121.filletArc", {"start": v(19.7, -99.67) * mm, "mid": v(23.85, -96.8) * mm, "end": v(24.6, -91.8) * mm});
            skPoint(sketch, "E122.visualSharp", {"position": v(-26.3, -98.14) * mm});
            skArc(sketch, "E122.filletArc", {"start": v(-24.6, -91.8) * mm, "mid": v(-23.85, -96.8) * mm, "end": v(-19.7, -99.67) * mm});
            skSolve(sketch);
        }
        {
            var Q0;
            Q0=qSketchRegion(id+"F2",true);
            extrude(context, id + "F3", {"entities" : qUnion([Q0]), "operationType" : NewBodyOperationType.REMOVE, "oppositeDirection" : true, "depth" : 3.17 * mm, "offsetDistance" : 25.4 * mm});
        }
        {
            var Q0;
            Q0=makeQuery(id+"F1.opExtrude","SWEPT_BODY",BODY,{"disambiguationData":[OSD([sQuery(id+"F0.wireOp",EDGE,"E0"),sQuery(id+"F0.wireOp",EDGE,"E1"),sQuery(id+"F0.wireOp",EDGE,"E2"),sQuery(id+"F0.wireOp",EDGE,"E3"),sQuery(id+"F0.wireOp",EDGE,"E4"),sQuery(id+"F0.wireOp",EDGE,"E5"),sQuery(id+"F0.wireOp",EDGE,"E6"),sQuery(id+"F0.wireOp",EDGE,"E7"),sQuery(id+"F0.wireOp",EDGE,"E8"),sQuery(id+"F0.wireOp",EDGE,"E9"),sQuery(id+"F0.wireOp",EDGE,"E10"),sQuery(id+"F0.wireOp",EDGE,"E11"),sQuery(id+"F0.wireOp",EDGE,"E12.trimOffspring"),sQuery(id+"F0.wireOp",EDGE,"E13.trimOffspring"),sQuery(id+"F0.wireOp",EDGE,"E14.trimOffspring"),sQuery(id+"F0.wireOp",EDGE,"E15.trimOffspring"),sQuery(id+"F0.wireOp",EDGE,"E16.trimOffspring"),sQuery(id+"F0.wireOp",EDGE,"E17.trimOffspring"),sQuery(id+"F0.wireOp",EDGE,"E18.filletArc"),sQuery(id+"F0.wireOp",EDGE,"E19.filletArc"),sQuery(id+"F0.wireOp",EDGE,"E20.filletArc"),sQuery(id+"F0.wireOp",EDGE,"E21.filletArc"),sQuery(id+"F0.wireOp",EDGE,"E22.filletArc"),sQuery(id+"F0.wireOp",EDGE,"E23.filletArc"),sQuery(id+"F0.wireOp",EDGE,"E24.filletArc"),sQuery(id+"F0.wireOp",EDGE,"E25.filletArc"),sQuery(id+"F0.wireOp",EDGE,"E26.filletArc"),sQuery(id+"F0.wireOp",EDGE,"E27.filletArc"),sQuery(id+"F0.wireOp",EDGE,"E28.filletArc"),sQuery(id+"F0.wireOp",EDGE,"E29.filletArc"),sQuery(id+"F0.wireOp",EDGE,"E30.filletArc"),sQuery(id+"F0.wireOp",EDGE,"E31.filletArc"),sQuery(id+"F0.wireOp",EDGE,"E32.filletArc"),sQuery(id+"F0.wireOp",EDGE,"E33.filletArc"),sQuery(id+"F0.wireOp",EDGE,"E34"),sQuery(id+"F0.wireOp",EDGE,"E35"),sQuery(id+"F0.wireOp",EDGE,"E36"),sQuery(id+"F0.wireOp",EDGE,"E37"),sQuery(id+"F0.wireOp",EDGE,"E38.trimOffspring"),sQuery(id+"F0.wireOp",EDGE,"E39.filletArc"),sQuery(id+"F0.wireOp",EDGE,"E40.filletArc"),sQuery(id+"F0.wireOp",EDGE,"E41.filletArc"),sQuery(id+"F0.wireOp",EDGE,"E42.filletArc"),sQuery(id+"F0.wireOp",EDGE,"E43.1.0"),sQuery(id+"F0.wireOp",EDGE,"E43.1.1"),sQuery(id+"F0.wireOp",EDGE,"E43.1.2"),sQuery(id+"F0.wireOp",EDGE,"E43.1.3"),sQuery(id+"F0.wireOp",EDGE,"E43.1.6"),sQuery(id+"F0.wireOp",EDGE,"E43.1.7"),sQuery(id+"F0.wireOp",EDGE,"E43.1.8"),sQuery(id+"F0.wireOp",EDGE,"E43.1.9"),sQuery(id+"F0.wireOp",EDGE,"E43.1.10"),sQuery(id+"F0.wireOp",EDGE,"E43.2.0"),sQuery(id+"F0.wireOp",EDGE,"E43.2.1"),sQuery(id+"F0.wireOp",EDGE,"E43.2.2"),sQuery(id+"F0.wireOp",EDGE,"E43.2.3"),sQuery(id+"F0.wireOp",EDGE,"E43.2.6"),sQuery(id+"F0.wireOp",EDGE,"E43.2.7"),sQuery(id+"F0.wireOp",EDGE,"E43.2.8"),sQuery(id+"F0.wireOp",EDGE,"E43.2.9"),sQuery(id+"F0.wireOp",EDGE,"E43.2.10"),sQuery(id+"F0.wireOp",EDGE,"E43.3.0"),sQuery(id+"F0.wireOp",EDGE,"E43.3.1"),sQuery(id+"F0.wireOp",EDGE,"E43.3.2"),sQuery(id+"F0.wireOp",EDGE,"E43.3.3"),sQuery(id+"F0.wireOp",EDGE,"E43.3.6"),sQuery(id+"F0.wireOp",EDGE,"E43.3.7"),sQuery(id+"F0.wireOp",EDGE,"E43.3.8"),sQuery(id+"F0.wireOp",EDGE,"E43.3.9"),sQuery(id+"F0.wireOp",EDGE,"E43.3.10"),sQuery(id+"F0.wireOp",EDGE,"E43.4.0"),sQuery(id+"F0.wireOp",EDGE,"E43.4.1"),sQuery(id+"F0.wireOp",EDGE,"E43.4.2"),sQuery(id+"F0.wireOp",EDGE,"E43.4.3"),sQuery(id+"F0.wireOp",EDGE,"E43.4.6"),sQuery(id+"F0.wireOp",EDGE,"E43.4.7"),sQuery(id+"F0.wireOp",EDGE,"E43.4.8"),sQuery(id+"F0.wireOp",EDGE,"E43.4.9"),sQuery(id+"F0.wireOp",EDGE,"E43.4.10"),sQuery(id+"F0.wireOp",EDGE,"E43.5.0"),sQuery(id+"F0.wireOp",EDGE,"E43.5.1"),sQuery(id+"F0.wireOp",EDGE,"E43.5.2"),sQuery(id+"F0.wireOp",EDGE,"E43.5.3"),sQuery(id+"F0.wireOp",EDGE,"E43.5.6"),sQuery(id+"F0.wireOp",EDGE,"E43.5.7"),sQuery(id+"F0.wireOp",EDGE,"E43.5.8"),sQuery(id+"F0.wireOp",EDGE,"E43.5.9"),sQuery(id+"F0.wireOp",EDGE,"E43.5.10"),sQuery(id+"F0.wireOp",EDGE,"E43.6.0"),sQuery(id+"F0.wireOp",EDGE,"E43.6.1"),sQuery(id+"F0.wireOp",EDGE,"E43.6.2"),sQuery(id+"F0.wireOp",EDGE,"E43.6.3"),sQuery(id+"F0.wireOp",EDGE,"E43.6.6"),sQuery(id+"F0.wireOp",EDGE,"E43.6.7"),sQuery(id+"F0.wireOp",EDGE,"E43.6.8"),sQuery(id+"F0.wireOp",EDGE,"E43.6.9"),sQuery(id+"F0.wireOp",EDGE,"E43.6.10"),sQuery(id+"F0.wireOp",EDGE,"E43.7.0"),sQuery(id+"F0.wireOp",EDGE,"E43.7.1"),sQuery(id+"F0.wireOp",EDGE,"E43.7.2"),sQuery(id+"F0.wireOp",EDGE,"E43.7.3"),sQuery(id+"F0.wireOp",EDGE,"E43.7.6"),sQuery(id+"F0.wireOp",EDGE,"E43.7.7"),sQuery(id+"F0.wireOp",EDGE,"E43.7.8"),sQuery(id+"F0.wireOp",EDGE,"E43.7.9"),sQuery(id+"F0.wireOp",EDGE,"E43.7.10"),sQuery(id+"F0.wireOp",EDGE,"E43.8.0"),sQuery(id+"F0.wireOp",EDGE,"E43.8.1"),sQuery(id+"F0.wireOp",EDGE,"E43.8.2"),sQuery(id+"F0.wireOp",EDGE,"E43.8.3"),sQuery(id+"F0.wireOp",EDGE,"E43.8.6"),sQuery(id+"F0.wireOp",EDGE,"E43.8.7"),sQuery(id+"F0.wireOp",EDGE,"E43.8.8"),sQuery(id+"F0.wireOp",EDGE,"E43.8.9"),sQuery(id+"F0.wireOp",EDGE,"E43.8.10"),sQuery(id+"F0.wireOp",EDGE,"E43.9.0"),sQuery(id+"F0.wireOp",EDGE,"E43.9.1"),sQuery(id+"F0.wireOp",EDGE,"E43.9.2"),sQuery(id+"F0.wireOp",EDGE,"E43.9.3"),sQuery(id+"F0.wireOp",EDGE,"E43.9.6"),sQuery(id+"F0.wireOp",EDGE,"E43.9.7"),sQuery(id+"F0.wireOp",EDGE,"E43.9.8"),sQuery(id+"F0.wireOp",EDGE,"E43.9.9"),sQuery(id+"F0.wireOp",EDGE,"E43.9.10"),sQuery(id+"F0.wireOp",EDGE,"E43.10.0"),sQuery(id+"F0.wireOp",EDGE,"E43.10.1"),sQuery(id+"F0.wireOp",EDGE,"E43.10.2"),sQuery(id+"F0.wireOp",EDGE,"E43.10.3"),sQuery(id+"F0.wireOp",EDGE,"E43.10.6"),sQuery(id+"F0.wireOp",EDGE,"E43.10.7"),sQuery(id+"F0.wireOp",EDGE,"E43.10.8"),sQuery(id+"F0.wireOp",EDGE,"E43.10.9"),sQuery(id+"F0.wireOp",EDGE,"E43.10.10"),sQuery(id+"F0.wireOp",EDGE,"E43.11.0"),sQuery(id+"F0.wireOp",EDGE,"E43.11.1"),sQuery(id+"F0.wireOp",EDGE,"E43.11.2"),sQuery(id+"F0.wireOp",EDGE,"E43.11.3"),sQuery(id+"F0.wireOp",EDGE,"E43.11.6"),sQuery(id+"F0.wireOp",EDGE,"E43.11.7"),sQuery(id+"F0.wireOp",EDGE,"E43.11.8"),sQuery(id+"F0.wireOp",EDGE,"E43.11.9"),sQuery(id+"F0.wireOp",EDGE,"E43.11.10"),sQuery(id+"F0.wireOp",EDGE,"E43.12.0"),sQuery(id+"F0.wireOp",EDGE,"E43.12.1"),sQuery(id+"F0.wireOp",EDGE,"E43.12.2"),sQuery(id+"F0.wireOp",EDGE,"E43.12.3"),sQuery(id+"F0.wireOp",EDGE,"E43.12.6"),sQuery(id+"F0.wireOp",EDGE,"E43.12.7"),sQuery(id+"F0.wireOp",EDGE,"E43.12.8"),sQuery(id+"F0.wireOp",EDGE,"E43.12.9"),sQuery(id+"F0.wireOp",EDGE,"E43.12.10"),sQuery(id+"F0.wireOp",EDGE,"E43.13.0"),sQuery(id+"F0.wireOp",EDGE,"E43.13.1"),sQuery(id+"F0.wireOp",EDGE,"E43.13.2"),sQuery(id+"F0.wireOp",EDGE,"E43.13.3"),sQuery(id+"F0.wireOp",EDGE,"E43.13.6"),sQuery(id+"F0.wireOp",EDGE,"E43.13.7"),sQuery(id+"F0.wireOp",EDGE,"E43.13.8"),sQuery(id+"F0.wireOp",EDGE,"E43.13.9"),sQuery(id+"F0.wireOp",EDGE,"E43.13.10"),sQuery(id+"F0.wireOp",EDGE,"E43.14.0"),sQuery(id+"F0.wireOp",EDGE,"E43.14.1"),sQuery(id+"F0.wireOp",EDGE,"E43.14.2"),sQuery(id+"F0.wireOp",EDGE,"E43.14.3"),sQuery(id+"F0.wireOp",EDGE,"E43.14.6"),sQuery(id+"F0.wireOp",EDGE,"E43.14.7"),sQuery(id+"F0.wireOp",EDGE,"E43.14.8"),sQuery(id+"F0.wireOp",EDGE,"E43.14.9"),sQuery(id+"F0.wireOp",EDGE,"E43.14.10"),sQuery(id+"F0.wireOp",EDGE,"E43.15.0"),sQuery(id+"F0.wireOp",EDGE,"E43.15.1"),sQuery(id+"F0.wireOp",EDGE,"E43.15.2"),sQuery(id+"F0.wireOp",EDGE,"E43.15.3"),sQuery(id+"F0.wireOp",EDGE,"E43.15.6"),sQuery(id+"F0.wireOp",EDGE,"E43.15.7"),sQuery(id+"F0.wireOp",EDGE,"E43.15.8"),sQuery(id+"F0.wireOp",EDGE,"E43.15.9"),sQuery(id+"F0.wireOp",EDGE,"E43.15.10"),sQuery(id+"F0.wireOp",EDGE,"E44.trimOffspring"),sQuery(id+"F0.wireOp",EDGE,"E45.trimOffspring"),sQuery(id+"F0.wireOp",EDGE,"E46.trimOffspring"),sQuery(id+"F0.wireOp",EDGE,"E47.trimOffspring"),sQuery(id+"F0.wireOp",EDGE,"E48.trimOffspring"),sQuery(id+"F0.wireOp",EDGE,"E49.trimOffspring"),sQuery(id+"F0.wireOp",EDGE,"E50.trimOffspring"),sQuery(id+"F0.wireOp",EDGE,"E51.trimOffspring"),sQuery(id+"F0.wireOp",EDGE,"E52.trimOffspring"),sQuery(id+"F0.wireOp",EDGE,"E53.trimOffspring"),sQuery(id+"F0.wireOp",EDGE,"E54.trimOffspring"),sQuery(id+"F0.wireOp",EDGE,"E55.trimOffspring"),sQuery(id+"F0.wireOp",EDGE,"E56.trimOffspring"),sQuery(id+"F0.wireOp",EDGE,"E57.trimOffspring"),sQuery(id+"F0.wireOp",EDGE,"E58.trimOffspring"),sQuery(id+"F0.wireOp",EDGE,"E59.filletArc"),sQuery(id+"F0.wireOp",EDGE,"E60.filletArc"),sQuery(id+"F0.wireOp",EDGE,"E61.filletArc"),sQuery(id+"F0.wireOp",EDGE,"E62.filletArc"),sQuery(id+"F0.wireOp",EDGE,"E63.filletArc"),sQuery(id+"F0.wireOp",EDGE,"E64.filletArc"),sQuery(id+"F0.wireOp",EDGE,"E65.filletArc"),sQuery(id+"F0.wireOp",EDGE,"E66.filletArc"),sQuery(id+"F0.wireOp",EDGE,"E67.filletArc"),sQuery(id+"F0.wireOp",EDGE,"E68.filletArc"),sQuery(id+"F0.wireOp",EDGE,"E69.filletArc"),sQuery(id+"F0.wireOp",EDGE,"E70.filletArc"),sQuery(id+"F0.wireOp",EDGE,"E71.filletArc"),sQuery(id+"F0.wireOp",EDGE,"E72.filletArc"),sQuery(id+"F0.wireOp",EDGE,"E73.filletArc"),sQuery(id+"F0.wireOp",EDGE,"E74.filletArc"),sQuery(id+"F0.wireOp",EDGE,"E75.filletArc"),sQuery(id+"F0.wireOp",EDGE,"E76.filletArc"),sQuery(id+"F0.wireOp",EDGE,"E77.filletArc"),sQuery(id+"F0.wireOp",EDGE,"E78.filletArc"),sQuery(id+"F0.wireOp",EDGE,"E79.filletArc"),sQuery(id+"F0.wireOp",EDGE,"E80.filletArc"),sQuery(id+"F0.wireOp",EDGE,"E81.filletArc"),sQuery(id+"F0.wireOp",EDGE,"E82.filletArc"),sQuery(id+"F0.wireOp",EDGE,"E83.filletArc"),sQuery(id+"F0.wireOp",EDGE,"E84.filletArc"),sQuery(id+"F0.wireOp",EDGE,"E85.filletArc"),sQuery(id+"F0.wireOp",EDGE,"E86.filletArc"),sQuery(id+"F0.wireOp",EDGE,"E87.filletArc"),sQuery(id+"F0.wireOp",EDGE,"E88.filletArc"),sQuery(id+"F0.wireOp",EDGE,"E89.filletArc"),sQuery(id+"F0.wireOp",EDGE,"E90.filletArc")])]});
            var Q1;
            Q1=makeQuery(id+"F1.opExtrude","CAP_EDGE",EDGE,{"disambiguationData":[OSD([sQuery(id+"F0.wireOp",EDGE,"E11")])],"isStart":false});
            transform(context, id + "F4", {"entities" : qUnion([Q0]), "transformType" : TransformType.ROTATION, "transformAxis" : qUnion([Q1]), "angle" : 11.25 * degree, "makeCopy" : false});
        }
    });
